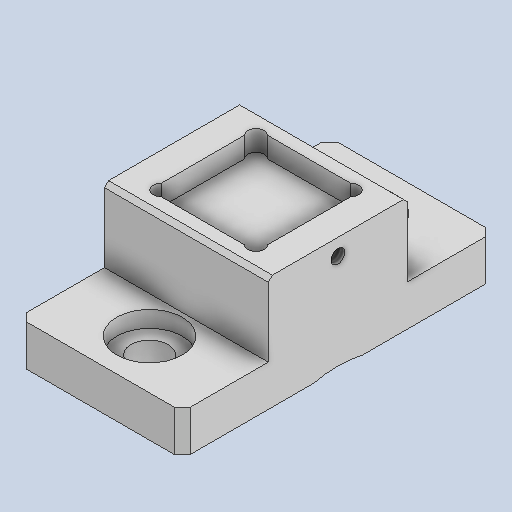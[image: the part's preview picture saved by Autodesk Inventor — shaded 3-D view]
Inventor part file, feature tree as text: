
AUTODESK INVENTOR PART (.ipt)
format: ipt  version: 2024.2 (Build 282272000, 272)  size: 311,808 bytes
history: native  units: in
note: dims shown in document units (in); Inventor stores cm internally (conversion verified against a paired STEP export)
features: extrude x6, other x4, hole x3, chamfer x2
ambient origin geometry x8: Origin, YZ Plane, XZ Plane, XY Plane, X Axis, Y Axis, Z Axis, Center Point
bodies: Solid1 (feature_tree)
feature tree (15):
  other  "Table"
  other  "ADAPTER_PBS-BH32-CS12.7"
  other  "ADAPTER_PBS-BH12.7-CS12.7"
  other  "ADAPTER_PBS-BH19.05-CS12.7"
  extrude  "Extrusion1"  TaperAngle=0.0deg  [1 undecoded]
  extrude  "Extrusion2"  TaperAngle=0.0deg  [1 undecoded]
  chamfer  "Chamfer6"  Distance=0.4134in
  hole  "Hole1"  [1 undecoded]
  extrude  "Extrusion8"  TaperAngle=0.0deg  [1 undecoded]
  chamfer  "Chamfer4"  Distance=0.2362in
  hole  "Hole6"  [1 undecoded]
  extrude  "Extrusion9"  Depth=0.3346in
  hole  "Hole7"  [1 undecoded]
  extrude  "Extrusion10"  Depth=0.0787in TaperAngle=45.0deg
  extrude  "Extrusion11"  Depth=0.0394in TaperAngle=45.0deg
note: 6 required parameter values undecoded (feature->parameter linkage not recoverable at this tier; creation-order binding heuristic only, values carry confidence <= 0.55)
